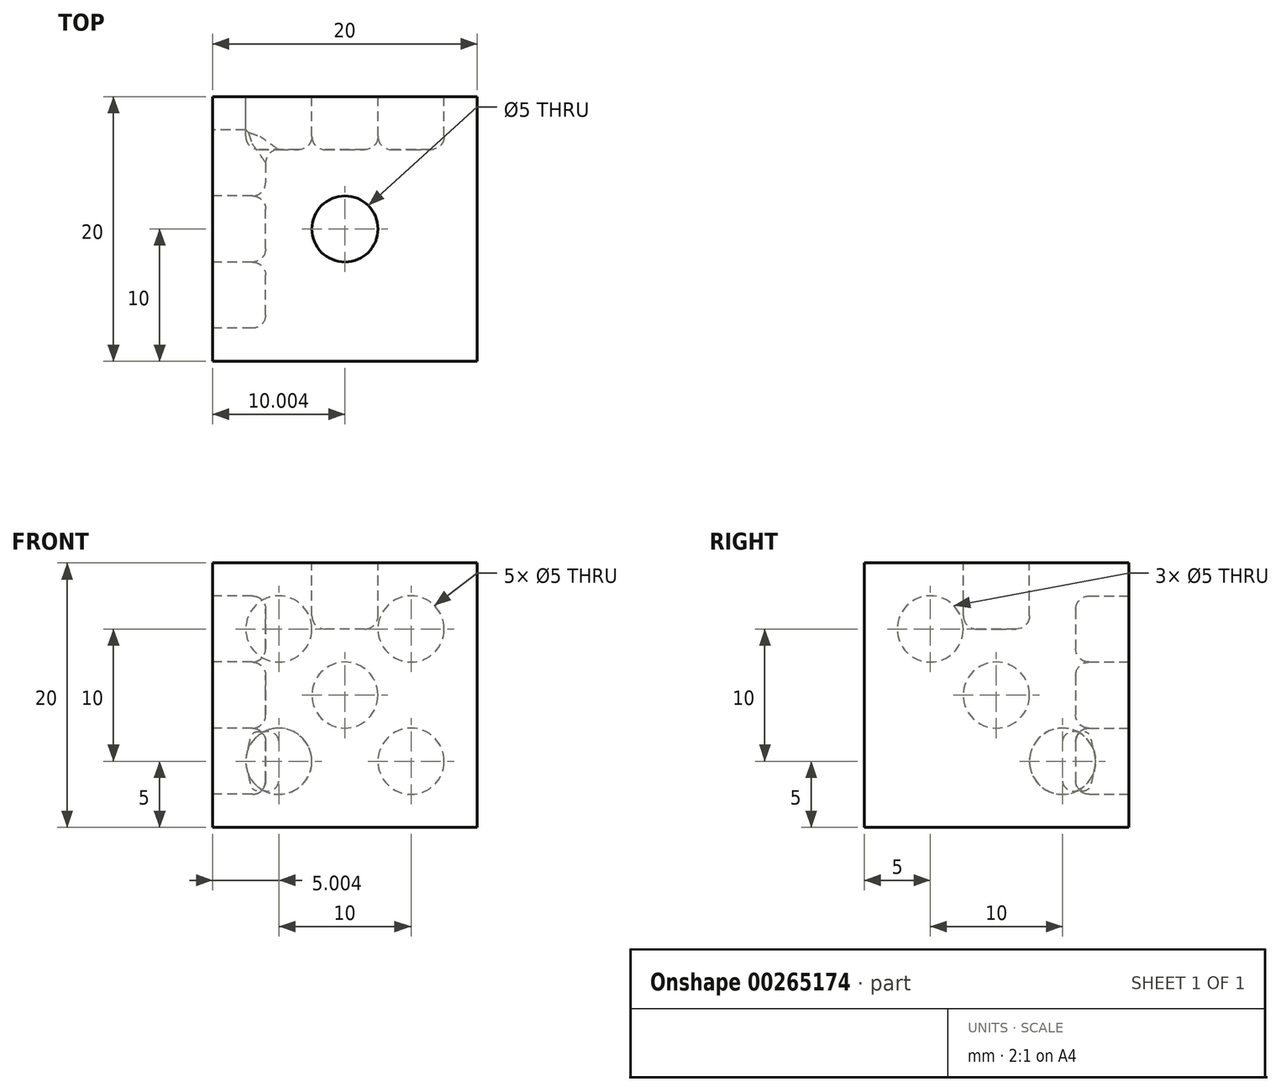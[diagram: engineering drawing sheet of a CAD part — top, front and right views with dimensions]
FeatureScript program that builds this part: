
annotation { "Feature Type Name" : "Feature", "Feature Type Description" : "" }
export const myFeature = defineFeature(function(context is Context, id is Id, definition is map)
    precondition{}
    {
        {
            var Q0;
            Q0=qCreatedBy(makeId("Top.planeOp"),FACE);
            var sketch = newSketch(context, id + "F0", { "sketchPlane" : qUnion([Q0])});
            skLineSegment(sketch, "E0.bottom", {"start": v(30.4, 20) * mm, "end": v(10.4, 20) * mm});
            skLineSegment(sketch, "E0.top", {"start": v(30.4, 0) * mm, "end": v(10.4, 0) * mm});
            skLineSegment(sketch, "E0.left", {"start": v(30.4, 20) * mm, "end": v(30.4, 0) * mm});
            skLineSegment(sketch, "E0.right", {"start": v(10.4, 20) * mm, "end": v(10.4, 0) * mm});
            skSolve(sketch);
        }
        {
            var Q0;
            Q0 = qSketchRegion(id + "F0", true);
            extrude(context, id + "F1", {"entities" : qUnion([Q0]), "depth" : 20 * mm});
        }
        {
            var Q0;
            Q0=makeQuery(id+"F1.opExtrude","CAP_FACE",FACE,{"disambiguationData":[OSD([sQuery(id+"F0.wireOp",EDGE,"E0.bottom"),sQuery(id+"F0.wireOp",EDGE,"E0.top"),sQuery(id+"F0.wireOp",EDGE,"E0.left"),sQuery(id+"F0.wireOp",EDGE,"E0.right")])],"isStart":false});
            var sketch = newSketch(context, id + "F2", { "sketchPlane" : qUnion([Q0])});
            skCircle(sketch, "E1", {"center": v(20.4, 10) * mm, "radius": 2.5 * mm});
            skSolve(sketch);
        }
        {
            var Q0;
            Q0=makeQuery(id+"F2.imprint","IMPRINT",FACE,{"disambiguationData":[TD([[makeQuery(id+"F2.imprint","IMPRINT",EDGE,{"derivedFrom":sQuery(id+"F2.wireOp",EDGE,"E1")}),1.0]])]});
            extrude(context, id + "F3", {"entities" : qUnion([Q0]), "operationType" : NewBodyOperationType.REMOVE, "oppositeDirection" : true, "depth" : 5 * mm});
        }
        {
            var Q0;
            Q0=makeQuery(id+"F3.boolean.opBoolean","COPY",FACE,{"derivedFrom":makeQuery(id+"F3.opExtrude","CAP_FACE",FACE,{"disambiguationData":[OSD([sQuery(id+"F2.wireOp",EDGE,"E1")])],"isStart":false})});
            fillet(context, id + "F4", {"entities" : qUnion([Q0]), "radius" : 1 * mm, "tangentPropagation" : true, "allowEdgeOverflow" : false});
        }
        {
            var Q0;
            Q0=makeQuery(id+"F1.opExtrude","SWEPT_FACE",FACE,{"disambiguationData":[OSD([sQuery(id+"F0.wireOp",EDGE,"E0.right")])]});
            var sketch = newSketch(context, id + "F5", { "sketchPlane" : qUnion([Q0])});
            skCircle(sketch, "E2", {"center": v(-10, 10) * mm, "radius": 2.5 * mm});
            skSolve(sketch);
        }
        {
            var Q0;
            Q0 = qSketchRegion(id + "F5", true);
            extrude(context, id + "F6", {"entities" : qUnion([Q0]), "operationType" : NewBodyOperationType.REMOVE, "oppositeDirection" : true, "depth" : 4 * mm});
        }
        {
            var Q0;
            Q0=makeQuery(id+"F6.boolean.opBoolean","COPY",FACE,{"derivedFrom":makeQuery(id+"F6.opExtrude","CAP_FACE",FACE,{"disambiguationData":[OSD([sQuery(id+"F5.wireOp",EDGE,"E2")])],"isStart":false})});
            fillet(context, id + "F7", {"entities" : qUnion([Q0]), "radius" : 1 * mm, "tangentPropagation" : true, "allowEdgeOverflow" : false});
        }
        {
            var Q0;
            Q0=makeQuery(id+"F1.opExtrude","SWEPT_FACE",FACE,{"disambiguationData":[OSD([sQuery(id+"F0.wireOp",EDGE,"E0.right")])]});
            var sketch = newSketch(context, id + "F8", { "sketchPlane" : qUnion([Q0])});
            skCircle(sketch, "E3", {"center": v(-5, 15) * mm, "radius": 2.5 * mm});
            skSolve(sketch);
        }
        {
            var Q0;
            Q0 = qSketchRegion(id + "F8", true);
            extrude(context, id + "F9", {"entities" : qUnion([Q0]), "operationType" : NewBodyOperationType.REMOVE, "oppositeDirection" : true, "depth" : 4 * mm});
        }
        {
            var Q0;
            Q0=makeQuery(id+"F9.boolean.opBoolean","COPY",FACE,{"derivedFrom":makeQuery(id+"F9.opExtrude","CAP_FACE",FACE,{"disambiguationData":[OSD([sQuery(id+"F8.wireOp",EDGE,"E3")])],"isStart":false})});
            fillet(context, id + "F10", {"entities" : qUnion([Q0]), "radius" : 1 * mm, "tangentPropagation" : true, "allowEdgeOverflow" : false});
        }
        {
            var Q0;
            Q0=makeQuery(id+"F1.opExtrude","SWEPT_FACE",FACE,{"disambiguationData":[OSD([sQuery(id+"F0.wireOp",EDGE,"E0.right")])]});
            var sketch = newSketch(context, id + "F11", { "sketchPlane" : qUnion([Q0])});
            skCircle(sketch, "E4", {"center": v(-15, 5) * mm, "radius": 2.5 * mm});
            skSolve(sketch);
        }
        {
            var Q0;
            Q0 = qSketchRegion(id + "F11", true);
            extrude(context, id + "F12", {"entities" : qUnion([Q0]), "operationType" : NewBodyOperationType.REMOVE, "oppositeDirection" : true, "depth" : 4 * mm});
        }
        {
            var Q0;
            Q0=makeQuery(id+"F12.boolean.opBoolean","COPY",EDGE,{"derivedFrom":makeQuery(id+"F12.opExtrude","CAP_EDGE",EDGE,{"disambiguationData":[OSD([sQuery(id+"F11.wireOp",EDGE,"E4")])],"isStart":false})});
            fillet(context, id + "F13", {"entities" : qUnion([Q0]), "radius" : 1 * mm, "tangentPropagation" : true, "allowEdgeOverflow" : false});
        }
        {
            var Q0;
            Q0=makeQuery(id+"F1.opExtrude","SWEPT_FACE",FACE,{"disambiguationData":[OSD([sQuery(id+"F0.wireOp",EDGE,"E0.bottom")])]});
            var sketch = newSketch(context, id + "F14", { "sketchPlane" : qUnion([Q0])});
            skCircle(sketch, "E5", {"center": v(-25.4, 15) * mm, "radius": 2.5 * mm});
            skCircle(sketch, "E6", {"center": v(-20.4, 10) * mm, "radius": 2.5 * mm});
            skCircle(sketch, "E7", {"center": v(-15.4, 15) * mm, "radius": 2.5 * mm});
            skCircle(sketch, "E8", {"center": v(-15.4, 5) * mm, "radius": 2.5 * mm});
            skCircle(sketch, "E9", {"center": v(-25.4, 5) * mm, "radius": 2.5 * mm});
            skSolve(sketch);
        }
        {
            var Q0;
            Q0=makeQuery(id+"F14.imprint","IMPRINT",FACE,{"disambiguationData":[TD([[makeQuery(id+"F14.imprint","IMPRINT",EDGE,{"derivedFrom":sQuery(id+"F14.wireOp",EDGE,"E5")}),1.0]])]});
            var Q1;
            Q1=makeQuery(id+"F14.imprint","IMPRINT",FACE,{"disambiguationData":[TD([[makeQuery(id+"F14.imprint","IMPRINT",EDGE,{"derivedFrom":sQuery(id+"F14.wireOp",EDGE,"E9")}),1.0]])]});
            var Q2;
            Q2=makeQuery(id+"F14.imprint","IMPRINT",FACE,{"disambiguationData":[TD([[makeQuery(id+"F14.imprint","IMPRINT",EDGE,{"derivedFrom":sQuery(id+"F14.wireOp",EDGE,"E6")}),1.0]])]});
            var Q3;
            Q3=makeQuery(id+"F14.imprint","IMPRINT",FACE,{"disambiguationData":[TD([[makeQuery(id+"F14.imprint","IMPRINT",EDGE,{"derivedFrom":sQuery(id+"F14.wireOp",EDGE,"E7")}),1.0]])]});
            var Q4;
            Q4=makeQuery(id+"F14.imprint","IMPRINT",FACE,{"disambiguationData":[TD([[makeQuery(id+"F14.imprint","IMPRINT",EDGE,{"derivedFrom":sQuery(id+"F14.wireOp",EDGE,"E8")}),1.0]])]});
            extrude(context, id + "F15", {"entities" : qUnion([Q0, Q1, Q2, Q3, Q4]), "operationType" : NewBodyOperationType.REMOVE, "oppositeDirection" : true, "depth" : 4 * mm});
        }
        {
            var Q0;
            Q0=makeQuery(id+"F15.boolean.opBoolean","COPY",FACE,{"derivedFrom":makeQuery(id+"F15.opExtrude","CAP_FACE",FACE,{"disambiguationData":[OSD([sQuery(id+"F14.wireOp",EDGE,"E9")])],"isStart":false})});
            var Q1;
            Q1=makeQuery(id+"F15.boolean.opBoolean","COPY",FACE,{"derivedFrom":makeQuery(id+"F15.opExtrude","CAP_FACE",FACE,{"disambiguationData":[OSD([sQuery(id+"F14.wireOp",EDGE,"E6")])],"isStart":false})});
            var Q2;
            Q2=makeQuery(id+"F15.boolean.opBoolean","COPY",FACE,{"derivedFrom":makeQuery(id+"F15.opExtrude","CAP_FACE",FACE,{"disambiguationData":[OSD([sQuery(id+"F14.wireOp",EDGE,"E5")])],"isStart":false})});
            var Q3;
            Q3=makeQuery(id+"F15.boolean.opBoolean","COPY",FACE,{"derivedFrom":makeQuery(id+"F15.opExtrude","CAP_FACE",FACE,{"disambiguationData":[OSD([sQuery(id+"F14.wireOp",EDGE,"E7")])],"isStart":false})});
            var Q4;
            Q4=makeQuery(id+"F15.boolean.opBoolean","COPY",FACE,{"derivedFrom":makeQuery(id+"F15.opExtrude","CAP_FACE",FACE,{"disambiguationData":[OSD([sQuery(id+"F14.wireOp",EDGE,"E8")])],"isStart":false})});
            fillet(context, id + "F16", {"entities" : qUnion([Q0, Q1, Q2, Q3, Q4]), "radius" : 1 * mm, "tangentPropagation" : true, "allowEdgeOverflow" : false});
        }
    });
